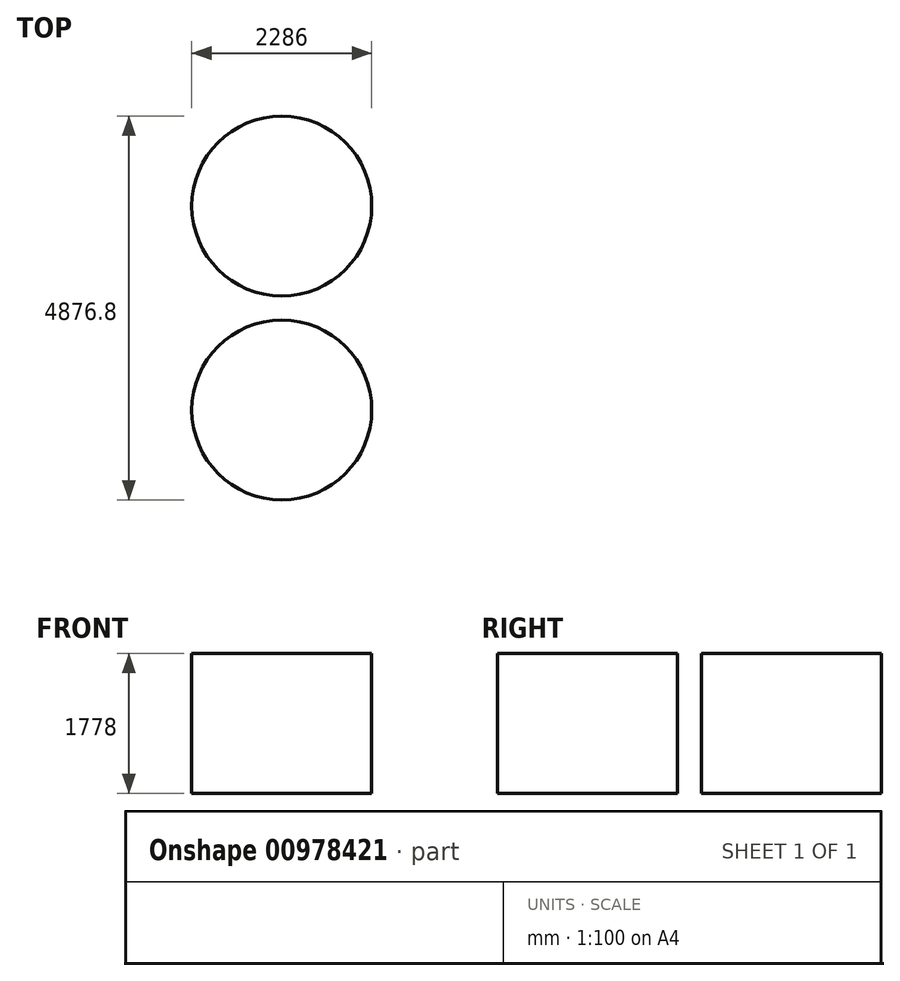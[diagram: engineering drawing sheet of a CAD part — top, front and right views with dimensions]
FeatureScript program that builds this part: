
annotation { "Feature Type Name" : "Feature", "Feature Type Description" : "" }
export const myFeature = defineFeature(function(context is Context, id is Id, definition is map)
    precondition{}
    {
        {
            var Q0;
            Q0=qCreatedBy(makeId("Top.planeOp"),FACE);
            var sketch = newSketch(context, id + "F0", { "sketchPlane" : qUnion([Q0])});
            skLineSegment(sketch, "E0", {"start": v(0, 0) * mm, "end": v(0, 1295.4) * mm});
            skLineSegment(sketch, "E1", {"start": v(0, 0) * mm, "end": v(0, -1295.4) * mm});
            skCircle(sketch, "E2", {"center": v(0, -1295.4) * mm, "radius": 1143 * mm});
            skCircle(sketch, "E3", {"center": v(0, 1295.4) * mm, "radius": 1143 * mm});
            skSolve(sketch);
        }
        {
            var Q0;
            Q0=makeQuery(id+"F0.imprint","IMPRINT",FACE,{"disambiguationData":[TD([[makeQuery(id+"F0.imprint","IMPRINT",EDGE,{"derivedFrom":sQuery(id+"F0.wireOp",EDGE,"E3")}),1.0]])]});
            var Q1;
            Q1=makeQuery(id+"F0.imprint","IMPRINT",FACE,{"disambiguationData":[TD([[makeQuery(id+"F0.imprint","IMPRINT",EDGE,{"derivedFrom":sQuery(id+"F0.wireOp",EDGE,"E2")}),1.0]])]});
            extrude(context, id + "F1", {"entities" : qUnion([Q0, Q1]), "depth" : 1778 * mm, "offsetDistance" : 25.4 * mm});
        }
    });
